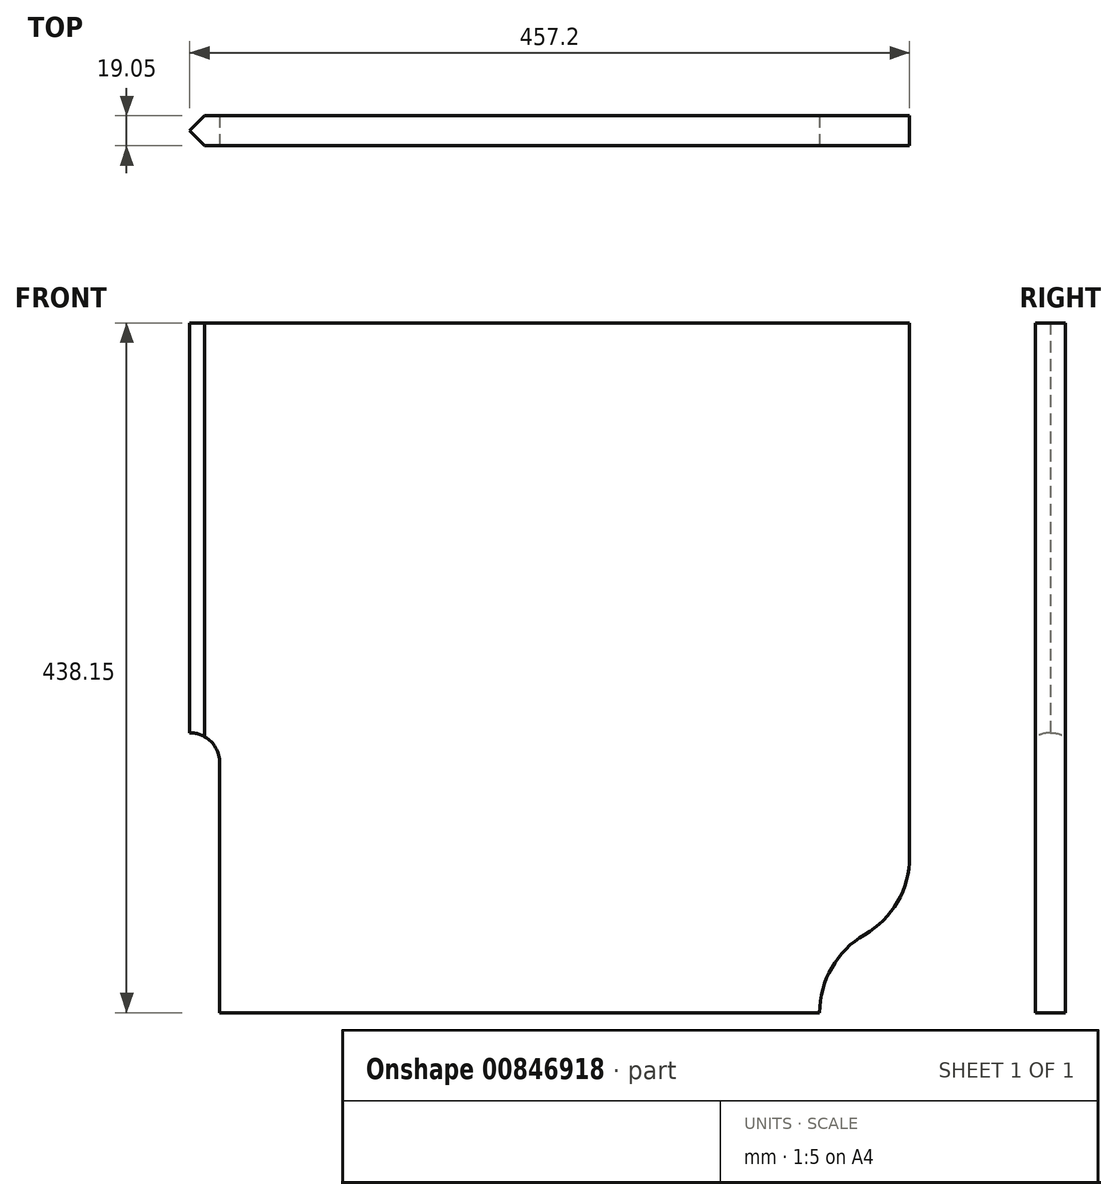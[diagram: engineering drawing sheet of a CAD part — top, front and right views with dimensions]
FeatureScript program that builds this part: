
annotation { "Feature Type Name" : "Feature", "Feature Type Description" : "" }
export const myFeature = defineFeature(function(context is Context, id is Id, definition is map)
    precondition{}
    {
        {
            var Q0;
            Q0=qCreatedBy(makeId("Front.planeOp"),FACE);
            var sketch = newSketch(context, id + "F0", { "sketchPlane" : qUnion([Q0])});
            skLineSegment(sketch, "E0.bottom", {"start": v(-155.23, 276.63) * mm, "end": v(301.97, 276.63) * mm});
            skLineSegment(sketch, "E0.top", {"start": v(-136.18, -161.52) * mm, "end": v(244.82, -161.52) * mm});
            skLineSegment(sketch, "E0.left", {"start": v(-155.23, 276.63) * mm, "end": v(-155.23, 16.28) * mm});
            skLineSegment(sketch, "E0.right", {"start": v(301.97, 276.63) * mm, "end": v(301.97, -62.53) * mm});
            skArc(sketch, "E1", {"start": v(273.4, -112.02) * mm, "mid": v(252.47, -132.94) * mm, "end": v(244.82, -161.52) * mm});
            skLineSegment(sketch, "E2.top", {"start": v(-155.23, 16.28) * mm, "end": v(-155.23, 16.28) * mm});
            skLineSegment(sketch, "E2.right", {"start": v(-136.18, -161.52) * mm, "end": v(-136.18, -2.77) * mm});
            skPoint(sketch, "E3.visualSharp", {"position": v(-136.18, 16.28) * mm});
            skArc(sketch, "E3.filletArc", {"start": v(-136.18, -2.77) * mm, "mid": v(-141.76, 10.7) * mm, "end": v(-155.23, 16.28) * mm});
            skPoint(sketch, "E4.visualSharp", {"position": v(301.97, -104.37) * mm});
            skArc(sketch, "E4.filletArc", {"start": v(273.4, -112.02) * mm, "mid": v(294.3, -91.1) * mm, "end": v(301.97, -62.53) * mm});
            skSolve(sketch);
        }
        {
            var Q0;
            Q0=makeQuery(id+"F0.imprint","IMPRINT",FACE,{"disambiguationData":[TD([[makeQuery(id+"F0.imprint","IMPRINT",EDGE,{"derivedFrom":sQuery(id+"F0.wireOp",EDGE,"E0.bottom")}),-1.0]])]});
            extrude(context, id + "F1", {"entities" : qUnion([Q0]), "oppositeDirection" : true, "depth" : 19.05 * mm, "offsetDistance" : 25.4 * mm});
        }
        {
            var Q0;
            Q0=makeQuery(id+"F1.opExtrude","CAP_EDGE",EDGE,{"disambiguationData":[OSD([sQuery(id+"F0.wireOp",EDGE,"E0.left")])],"isStart":true});
            var Q1;
            Q1=makeQuery(id+"F1.opExtrude","CAP_EDGE",EDGE,{"disambiguationData":[OSD([sQuery(id+"F0.wireOp",EDGE,"E0.left")])],"isStart":false});
            chamfer(context, id + "F2", {"entities" : qUnion([Q0, Q1]), "width" : 9.52 * mm, "tangentPropagation" : true});
        }
    });
